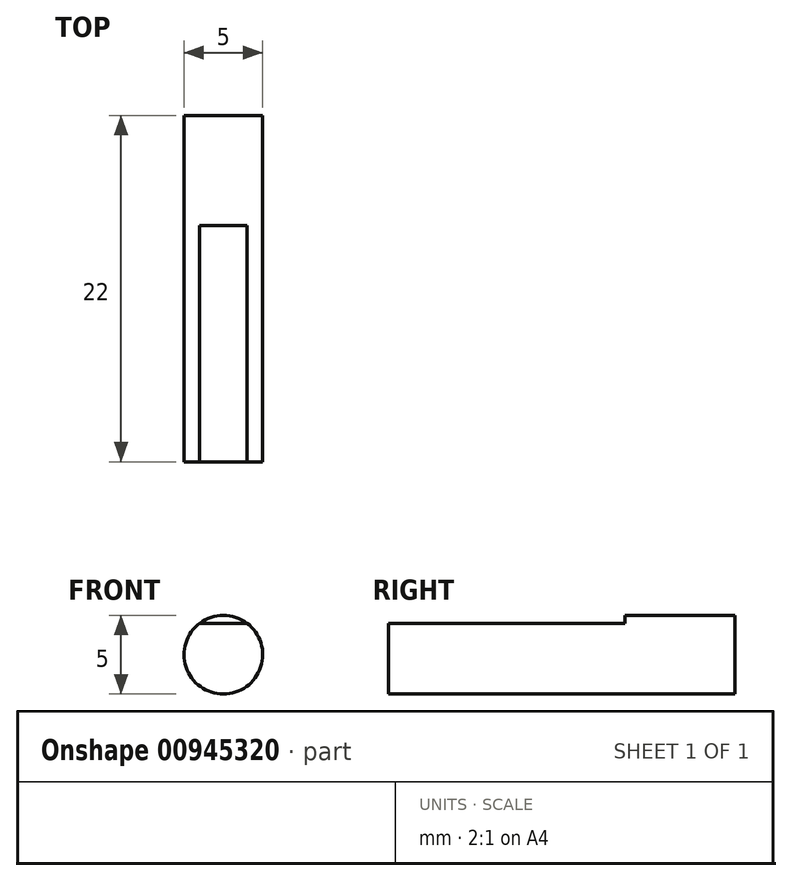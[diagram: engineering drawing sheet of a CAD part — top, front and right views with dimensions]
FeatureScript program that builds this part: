
annotation { "Feature Type Name" : "Feature", "Feature Type Description" : "" }
export const myFeature = defineFeature(function(context is Context, id is Id, definition is map)
    precondition{}
    {
        {
            var Q0;
            Q0=qCreatedBy(makeId("Front.planeOp"),FACE);
            var sketch = newSketch(context, id + "F0", { "sketchPlane" : qUnion([Q0])});
            skLineSegment(sketch, "E0.bottom", {"start": v(-21.15, 21.15) * mm, "end": v(21.15, 21.15) * mm});
            skLineSegment(sketch, "E0.top", {"start": v(-21.15, -21.15) * mm, "end": v(21.15, -21.15) * mm});
            skLineSegment(sketch, "E0.left", {"start": v(-21.15, 21.15) * mm, "end": v(-21.15, -21.15) * mm});
            skLineSegment(sketch, "E0.right", {"start": v(21.15, 21.15) * mm, "end": v(21.15, -21.15) * mm});
            skPoint(sketch, "E1", {"position": v(0, 0) * mm});
            skSolve(sketch);
        }
        {
            var Q0;
            Q0=makeQuery(id+"F0.imprint","IMPRINT",FACE,{"disambiguationData":[TD([[makeQuery(id+"F0.imprint","IMPRINT",EDGE,{"derivedFrom":sQuery(id+"F0.wireOp",EDGE,"E0.bottom")}),-1.0]])]});
            extrude(context, id + "F1", {"entities" : qUnion([Q0]), "depth" : 59 * mm});
        }
        {
            var Q0;
            Q0=makeQuery(id+"F1.opExtrude","CAP_FACE",FACE,{"disambiguationData":[OSD([sQuery(id+"F0.wireOp",EDGE,"E0.bottom"),sQuery(id+"F0.wireOp",EDGE,"E0.top"),sQuery(id+"F0.wireOp",EDGE,"E0.left"),sQuery(id+"F0.wireOp",EDGE,"E0.right")])],"isStart":false});
            var sketch = newSketch(context, id + "F2", { "sketchPlane" : qUnion([Q0])});
            skCircle(sketch, "E2", {"center": v(0, 0) * mm, "radius": 11 * mm});
            skSolve(sketch);
        }
        {
            var Q0;
            Q0=makeQuery(id+"F2.imprint","IMPRINT",FACE,{"disambiguationData":[TD([[makeQuery(id+"F2.imprint","IMPRINT",EDGE,{"derivedFrom":sQuery(id+"F2.wireOp",EDGE,"E2")}),1.0]])]});
            extrude(context, id + "F3", {"entities" : qUnion([Q0]), "operationType" : NewBodyOperationType.ADD, "depth" : 2 * mm});
        }
        {
            var Q0;
            Q0=makeQuery(id+"F3.opExtrude","CAP_FACE",FACE,{"disambiguationData":[OSD([sQuery(id+"F2.wireOp",EDGE,"E2")])],"isStart":false});
            var sketch = newSketch(context, id + "F4", { "sketchPlane" : qUnion([Q0])});
            skCircle(sketch, "E3", {"center": v(0, 0) * mm, "radius": 2.5 * mm});
            skSolve(sketch);
        }
        {
            var Q0;
            Q0=makeQuery(id+"F4.imprint","IMPRINT",FACE,{"disambiguationData":[TD([[makeQuery(id+"F4.imprint","IMPRINT",EDGE,{"derivedFrom":sQuery(id+"F4.wireOp",EDGE,"E3")}),1.0]])]});
            extrude(context, id + "F5", {"entities" : qUnion([Q0]), "operationType" : NewBodyOperationType.ADD, "depth" : 22 * mm});
        }
        {
            var Q0;
            Q0=makeQuery(id+"F5.opExtrude","CAP_FACE",FACE,{"disambiguationData":[OSD([sQuery(id+"F4.wireOp",EDGE,"E3")])],"isStart":false});
            var sketch = newSketch(context, id + "F6", { "sketchPlane" : qUnion([Q0])});
            skLineSegment(sketch, "E4", {"start": v(-1.5, 2) * mm, "end": v(1.5, 2) * mm});
            skLineSegment(sketch, "E5", {"start": v(0, 2.5) * mm, "end": v(0, 2) * mm});
            skSolve(sketch);
        }
        {
            var Q0;
            {var subQ3=sQuery(id+"F6.wireOp",EDGE,"E5");Q0=makeQuery(id+"F6.imprint","IMPRINT",FACE,{"disambiguationData":[TD([[makeQuery(id+"F6.imprint","IMPRINT",EDGE,{"derivedFrom":subQ3}),-1.0]])]});}
            var Q1;
            {var subQ3=sQuery(id+"F6.wireOp",EDGE,"E5");Q1=makeQuery(id+"F6.imprint","IMPRINT",FACE,{"disambiguationData":[TD([[makeQuery(id+"F6.imprint","IMPRINT",EDGE,{"derivedFrom":subQ3}),1.0]])]});}
            extrude(context, id + "F7", {"entities" : qUnion([Q0, Q1]), "operationType" : NewBodyOperationType.REMOVE, "oppositeDirection" : true, "depth" : 15 * mm});
        }
        {
            var Q0;
            Q0=makeQuery(id+"F1.opExtrude","CAP_FACE",FACE,{"disambiguationData":[OSD([sQuery(id+"F0.wireOp",EDGE,"E0.bottom"),sQuery(id+"F0.wireOp",EDGE,"E0.top"),sQuery(id+"F0.wireOp",EDGE,"E0.left"),sQuery(id+"F0.wireOp",EDGE,"E0.right")])],"isStart":false});
            var sketch = newSketch(context, id + "F8", { "sketchPlane" : qUnion([Q0])});
            skLineSegment(sketch, "E6.bottom", {"start": v(-15.5, 15.5) * mm, "end": v(15.5, 15.5) * mm});
            skLineSegment(sketch, "E6.top", {"start": v(-15.5, -15.5) * mm, "end": v(15.5, -15.5) * mm});
            skLineSegment(sketch, "E6.left", {"start": v(-15.5, 15.5) * mm, "end": v(-15.5, -15.5) * mm});
            skLineSegment(sketch, "E6.right", {"start": v(15.5, 15.5) * mm, "end": v(15.5, -15.5) * mm});
            skPoint(sketch, "E7", {"position": v(0, 0) * mm});
            skCircle(sketch, "E8", {"center": v(-15.5, 15.5) * mm, "radius": 1.25 * mm});
            skCircle(sketch, "E9", {"center": v(15.5, 15.5) * mm, "radius": 1.25 * mm});
            skCircle(sketch, "E10", {"center": v(-15.5, -15.5) * mm, "radius": 1.25 * mm});
            skCircle(sketch, "E11", {"center": v(15.5, -15.5) * mm, "radius": 1.25 * mm});
            skSolve(sketch);
        }
        {
            var Q0;
            {var subQ0=sQuery(id+"F8.wireOp",EDGE,"E6.right");var subQ1=sQuery(id+"F8.wireOp",EDGE,"E6.bottom");var subQ2=makeQuery(id+"F8.imprint","INTERSECT",VERTEX,{"derivedFrom":[subQ1,subQ0]});Q0=makeQuery(id+"F8.imprint","IMPRINT",FACE,{"disambiguationData":[TD([[makeQuery(id+"F8.imprint","IMPRINT",EDGE,{"disambiguationData":[TD([[subQ2,1.0]])],"derivedFrom":subQ1}),1.0]])]});}
            var Q1;
            {var subQ0=sQuery(id+"F8.wireOp",EDGE,"E6.right");var subQ1=sQuery(id+"F8.wireOp",EDGE,"E6.bottom");var subQ2=makeQuery(id+"F8.imprint","INTERSECT",VERTEX,{"derivedFrom":[subQ1,subQ0]});Q1=makeQuery(id+"F8.imprint","IMPRINT",FACE,{"disambiguationData":[TD([[makeQuery(id+"F8.imprint","IMPRINT",EDGE,{"disambiguationData":[TD([[subQ2,1.0]])],"derivedFrom":subQ1}),-1.0]])]});}
            var Q2;
            {var subQ0=sQuery(id+"F8.wireOp",EDGE,"E6.left");var subQ1=sQuery(id+"F8.wireOp",EDGE,"E6.bottom");var subQ2=makeQuery(id+"F8.imprint","INTERSECT",VERTEX,{"derivedFrom":[subQ1,subQ0]});Q2=makeQuery(id+"F8.imprint","IMPRINT",FACE,{"disambiguationData":[TD([[makeQuery(id+"F8.imprint","IMPRINT",EDGE,{"disambiguationData":[TD([[subQ2,-1.0]])],"derivedFrom":subQ1}),1.0]])]});}
            var Q3;
            {var subQ0=sQuery(id+"F8.wireOp",EDGE,"E6.left");var subQ1=sQuery(id+"F8.wireOp",EDGE,"E6.bottom");var subQ2=makeQuery(id+"F8.imprint","INTERSECT",VERTEX,{"derivedFrom":[subQ1,subQ0]});Q3=makeQuery(id+"F8.imprint","IMPRINT",FACE,{"disambiguationData":[TD([[makeQuery(id+"F8.imprint","IMPRINT",EDGE,{"disambiguationData":[TD([[subQ2,-1.0]])],"derivedFrom":subQ1}),-1.0]])]});}
            var Q4;
            {var subQ0=sQuery(id+"F8.wireOp",EDGE,"E6.left");var subQ1=sQuery(id+"F8.wireOp",EDGE,"E6.top");var subQ2=makeQuery(id+"F8.imprint","INTERSECT",VERTEX,{"derivedFrom":[subQ1,subQ0]});Q4=makeQuery(id+"F8.imprint","IMPRINT",FACE,{"disambiguationData":[TD([[makeQuery(id+"F8.imprint","IMPRINT",EDGE,{"disambiguationData":[TD([[subQ2,-1.0]])],"derivedFrom":subQ1}),-1.0]])]});}
            var Q5;
            {var subQ0=sQuery(id+"F8.wireOp",EDGE,"E6.left");var subQ1=sQuery(id+"F8.wireOp",EDGE,"E6.top");var subQ2=makeQuery(id+"F8.imprint","INTERSECT",VERTEX,{"derivedFrom":[subQ1,subQ0]});Q5=makeQuery(id+"F8.imprint","IMPRINT",FACE,{"disambiguationData":[TD([[makeQuery(id+"F8.imprint","IMPRINT",EDGE,{"disambiguationData":[TD([[subQ2,-1.0]])],"derivedFrom":subQ1}),1.0]])]});}
            var Q6;
            {var subQ0=sQuery(id+"F8.wireOp",EDGE,"E6.right");var subQ1=sQuery(id+"F8.wireOp",EDGE,"E6.top");var subQ2=makeQuery(id+"F8.imprint","INTERSECT",VERTEX,{"derivedFrom":[subQ1,subQ0]});Q6=makeQuery(id+"F8.imprint","IMPRINT",FACE,{"disambiguationData":[TD([[makeQuery(id+"F8.imprint","IMPRINT",EDGE,{"disambiguationData":[TD([[subQ2,1.0]])],"derivedFrom":subQ1}),1.0]])]});}
            var Q7;
            {var subQ0=sQuery(id+"F8.wireOp",EDGE,"E6.right");var subQ1=sQuery(id+"F8.wireOp",EDGE,"E6.top");var subQ2=makeQuery(id+"F8.imprint","INTERSECT",VERTEX,{"derivedFrom":[subQ1,subQ0]});Q7=makeQuery(id+"F8.imprint","IMPRINT",FACE,{"disambiguationData":[TD([[makeQuery(id+"F8.imprint","IMPRINT",EDGE,{"disambiguationData":[TD([[subQ2,1.0]])],"derivedFrom":subQ1}),-1.0]])]});}
            extrude(context, id + "F9", {"entities" : qUnion([Q0, Q1, Q2, Q3, Q4, Q5, Q6, Q7]), "operationType" : NewBodyOperationType.REMOVE, "oppositeDirection" : true, "depth" : 4.5 * mm});
        }
        {
            var Q0;
            Q0=makeQuery(id+"F1.opExtrude","CAP_FACE",FACE,{"disambiguationData":[OSD([sQuery(id+"F0.wireOp",EDGE,"E0.bottom"),sQuery(id+"F0.wireOp",EDGE,"E0.top"),sQuery(id+"F0.wireOp",EDGE,"E0.left"),sQuery(id+"F0.wireOp",EDGE,"E0.right")])],"isStart":true});
            extrude(context, id + "F10", {"entities" : qUnion([Q0]), "operationType" : NewBodyOperationType.REMOVE, "oppositeDirection" : true, "depth" : 61 * mm, "offsetDistance" : 25 * mm});
        }
    });
